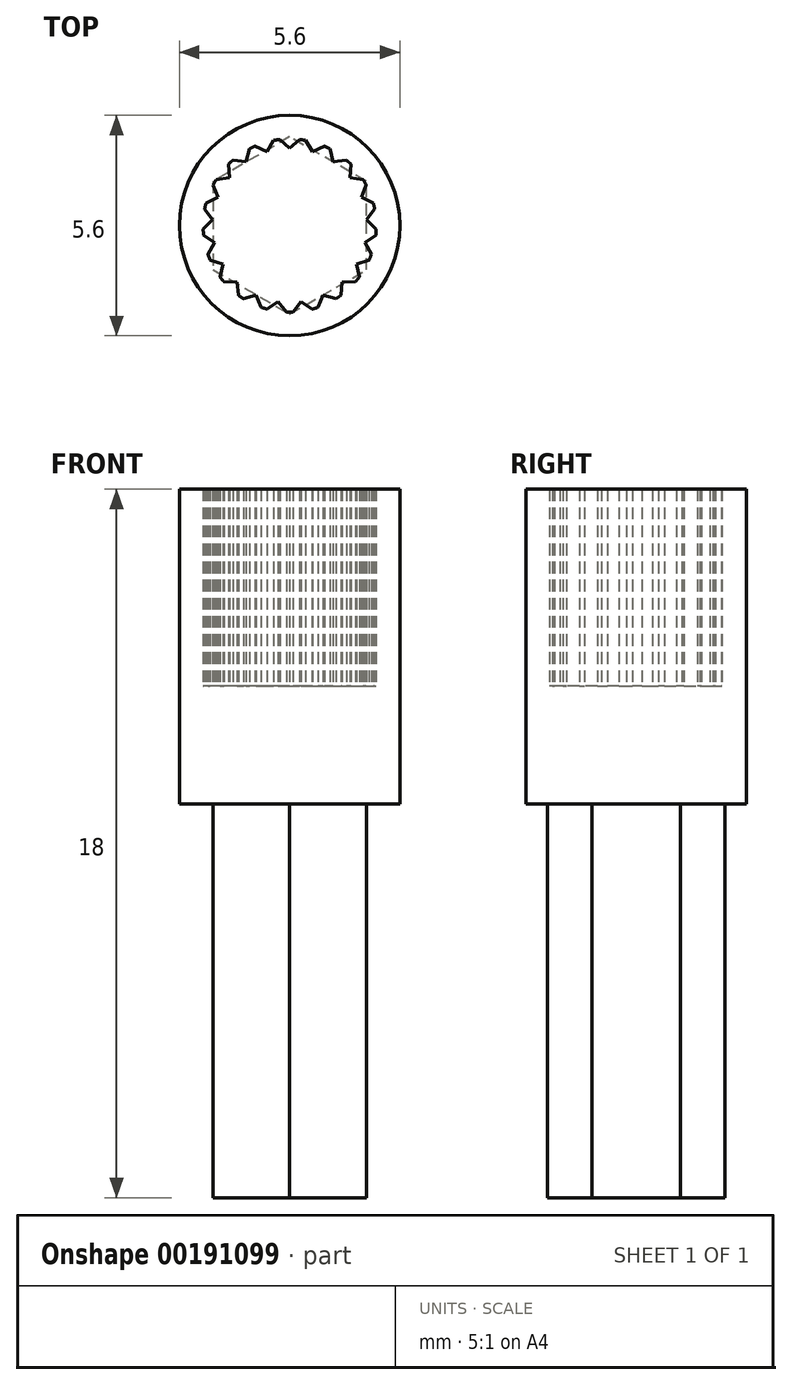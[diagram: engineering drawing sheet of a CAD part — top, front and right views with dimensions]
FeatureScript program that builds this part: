
annotation { "Feature Type Name" : "Feature", "Feature Type Description" : "" }
export const myFeature = defineFeature(function(context is Context, id is Id, definition is map)
    precondition{}
    {
        {
            var Q0;
            Q0=qCreatedBy(makeId("Top.planeOp"),FACE);
            var sketch = newSketch(context, id + "F0", { "sketchPlane" : qUnion([Q0])});
            skCircle(sketch, "E0", {"center": v(0, 0) * mm, "radius": 2.8 * mm});
            skLineSegment(sketch, "E1", {"start": v(0, 2.2) * mm, "end": v(0, 1.96) * mm, "construction": true});
            skArc(sketch, "E2", {"start": v(-0.25, 2.19) * mm, "mid": v(-0.33, 2.18) * mm, "end": v(-0.4, 2.16) * mm});
            skLineSegment(sketch, "E3", {"start": v(0, 1.96) * mm, "end": v(0.25, 2.19) * mm});
            skLineSegment(sketch, "E4.MirrorCS", {"start": v(0, 1.96) * mm, "end": v(-0.25, 2.19) * mm});
            skLineSegment(sketch, "E5.1.0", {"start": v(-0.58, 1.87) * mm, "end": v(-0.88, 2.01) * mm});
            skLineSegment(sketch, "E5.1.1", {"start": v(-0.58, 1.87) * mm, "end": v(-0.4, 2.16) * mm});
            skLineSegment(sketch, "E5.2.0", {"start": v(-1.1, 1.62) * mm, "end": v(-1.44, 1.66) * mm});
            skLineSegment(sketch, "E5.2.1", {"start": v(-1.1, 1.62) * mm, "end": v(-1.02, 1.95) * mm});
            skLineSegment(sketch, "E5.3.0", {"start": v(-1.53, 1.22) * mm, "end": v(-1.86, 1.17) * mm});
            skLineSegment(sketch, "E5.3.1", {"start": v(-1.53, 1.22) * mm, "end": v(-1.55, 1.56) * mm});
            skLineSegment(sketch, "E5.4.0", {"start": v(-1.82, 0.72) * mm, "end": v(-2.13, 0.57) * mm});
            skLineSegment(sketch, "E5.4.1", {"start": v(-1.82, 0.72) * mm, "end": v(-1.94, 1.03) * mm});
            skLineSegment(sketch, "E5.5.0", {"start": v(-1.95, 0.15) * mm, "end": v(-2.2, -0.09) * mm});
            skLineSegment(sketch, "E5.5.1", {"start": v(-1.95, 0.15) * mm, "end": v(-2.16, 0.41) * mm});
            skLineSegment(sketch, "E5.6.0", {"start": v(-1.91, -0.44) * mm, "end": v(-2.08, -0.73) * mm});
            skLineSegment(sketch, "E5.6.1", {"start": v(-1.91, -0.44) * mm, "end": v(-2.19, -0.24) * mm});
            skLineSegment(sketch, "E5.7.0", {"start": v(-1.7, -0.98) * mm, "end": v(-1.77, -1.3) * mm});
            skLineSegment(sketch, "E5.7.1", {"start": v(-1.7, -0.98) * mm, "end": v(-2.02, -0.88) * mm});
            skLineSegment(sketch, "E5.8.0", {"start": v(-1.33, -1.44) * mm, "end": v(-1.3, -1.77) * mm});
            skLineSegment(sketch, "E5.8.1", {"start": v(-1.33, -1.44) * mm, "end": v(-1.67, -1.43) * mm});
            skLineSegment(sketch, "E5.9.0", {"start": v(-0.85, -1.77) * mm, "end": v(-0.72, -2.08) * mm});
            skLineSegment(sketch, "E5.9.1", {"start": v(-0.85, -1.77) * mm, "end": v(-1.17, -1.86) * mm});
            skLineSegment(sketch, "E5.10.0", {"start": v(-0.3, -1.94) * mm, "end": v(-0.08, -2.2) * mm});
            skLineSegment(sketch, "E5.10.1", {"start": v(-0.3, -1.94) * mm, "end": v(-0.57, -2.12) * mm});
            skLineSegment(sketch, "E5.11.0", {"start": v(0.3, -1.94) * mm, "end": v(0.57, -2.12) * mm});
            skLineSegment(sketch, "E5.11.1", {"start": v(0.3, -1.94) * mm, "end": v(0.08, -2.2) * mm});
            skLineSegment(sketch, "E5.12.0", {"start": v(0.85, -1.77) * mm, "end": v(1.17, -1.86) * mm});
            skLineSegment(sketch, "E5.12.1", {"start": v(0.85, -1.77) * mm, "end": v(0.72, -2.08) * mm});
            skLineSegment(sketch, "E5.13.0", {"start": v(1.33, -1.44) * mm, "end": v(1.67, -1.43) * mm});
            skLineSegment(sketch, "E5.13.1", {"start": v(1.33, -1.44) * mm, "end": v(1.3, -1.77) * mm});
            skLineSegment(sketch, "E5.14.0", {"start": v(1.7, -0.98) * mm, "end": v(2.02, -0.88) * mm});
            skLineSegment(sketch, "E5.14.1", {"start": v(1.7, -0.98) * mm, "end": v(1.77, -1.3) * mm});
            skLineSegment(sketch, "E5.15.0", {"start": v(1.91, -0.44) * mm, "end": v(2.19, -0.24) * mm});
            skLineSegment(sketch, "E5.15.1", {"start": v(1.91, -0.44) * mm, "end": v(2.08, -0.73) * mm});
            skLineSegment(sketch, "E5.16.0", {"start": v(1.95, 0.15) * mm, "end": v(2.16, 0.41) * mm});
            skLineSegment(sketch, "E5.16.1", {"start": v(1.95, 0.15) * mm, "end": v(2.2, -0.09) * mm});
            skLineSegment(sketch, "E5.17.0", {"start": v(1.82, 0.72) * mm, "end": v(1.94, 1.03) * mm});
            skLineSegment(sketch, "E5.17.1", {"start": v(1.82, 0.72) * mm, "end": v(2.13, 0.57) * mm});
            skLineSegment(sketch, "E5.18.0", {"start": v(1.53, 1.22) * mm, "end": v(1.55, 1.56) * mm});
            skLineSegment(sketch, "E5.18.1", {"start": v(1.53, 1.22) * mm, "end": v(1.86, 1.17) * mm});
            skLineSegment(sketch, "E5.19.0", {"start": v(1.1, 1.62) * mm, "end": v(1.02, 1.95) * mm});
            skLineSegment(sketch, "E5.19.1", {"start": v(1.1, 1.62) * mm, "end": v(1.44, 1.66) * mm});
            skLineSegment(sketch, "E5.20.0", {"start": v(0.58, 1.87) * mm, "end": v(0.4, 2.16) * mm});
            skLineSegment(sketch, "E5.20.1", {"start": v(0.58, 1.87) * mm, "end": v(0.88, 2.01) * mm});
            skArc(sketch, "E6.trimOffspring", {"start": v(-0.88, 2.01) * mm, "mid": v(-0.95, 1.98) * mm, "end": v(-1.02, 1.95) * mm});
            skArc(sketch, "E7.trimOffspring", {"start": v(-1.44, 1.66) * mm, "mid": v(-1.5, 1.61) * mm, "end": v(-1.55, 1.56) * mm});
            skArc(sketch, "E8.trimOffspring", {"start": v(0.4, 2.16) * mm, "mid": v(0.33, 2.18) * mm, "end": v(0.25, 2.19) * mm});
            skArc(sketch, "E9.trimOffspring", {"start": v(1.02, 1.95) * mm, "mid": v(0.95, 1.98) * mm, "end": v(0.88, 2.01) * mm});
            skArc(sketch, "E10.trimOffspring", {"start": v(1.55, 1.56) * mm, "mid": v(1.5, 1.61) * mm, "end": v(1.44, 1.66) * mm});
            skArc(sketch, "E11.trimOffspring", {"start": v(1.94, 1.03) * mm, "mid": v(1.9, 1.1) * mm, "end": v(1.86, 1.17) * mm});
            skArc(sketch, "E12.trimOffspring", {"start": v(2.16, 0.41) * mm, "mid": v(2.14, 0.49) * mm, "end": v(2.13, 0.57) * mm});
            skArc(sketch, "E13.trimOffspring", {"start": v(2.19, -0.24) * mm, "mid": v(2.2, -0.16) * mm, "end": v(2.2, -0.09) * mm});
            skArc(sketch, "E14.trimOffspring", {"start": v(2.02, -0.88) * mm, "mid": v(2.05, -0.8) * mm, "end": v(2.08, -0.73) * mm});
            skArc(sketch, "E15.trimOffspring", {"start": v(1.67, -1.43) * mm, "mid": v(1.72, -1.37) * mm, "end": v(1.77, -1.3) * mm});
            skArc(sketch, "E16.trimOffspring", {"start": v(1.17, -1.86) * mm, "mid": v(1.24, -1.82) * mm, "end": v(1.3, -1.77) * mm});
            skArc(sketch, "E17.trimOffspring", {"start": v(0.57, -2.12) * mm, "mid": v(0.65, -2.1) * mm, "end": v(0.72, -2.08) * mm});
            skArc(sketch, "E18.trimOffspring", {"start": v(-0.08, -2.2) * mm, "mid": v(0, -2.2) * mm, "end": v(0.08, -2.2) * mm});
            skArc(sketch, "E19.trimOffspring", {"start": v(-0.72, -2.08) * mm, "mid": v(-0.65, -2.1) * mm, "end": v(-0.57, -2.12) * mm});
            skArc(sketch, "E20.trimOffspring", {"start": v(-1.3, -1.77) * mm, "mid": v(-1.24, -1.82) * mm, "end": v(-1.17, -1.86) * mm});
            skArc(sketch, "E21.trimOffspring", {"start": v(-1.77, -1.3) * mm, "mid": v(-1.72, -1.37) * mm, "end": v(-1.67, -1.43) * mm});
            skArc(sketch, "E22.trimOffspring", {"start": v(-2.08, -0.73) * mm, "mid": v(-2.05, -0.8) * mm, "end": v(-2.02, -0.88) * mm});
            skArc(sketch, "E23.trimOffspring", {"start": v(-2.2, -0.09) * mm, "mid": v(-2.2, -0.16) * mm, "end": v(-2.19, -0.24) * mm});
            skArc(sketch, "E24.trimOffspring", {"start": v(-2.13, 0.57) * mm, "mid": v(-2.14, 0.49) * mm, "end": v(-2.16, 0.41) * mm});
            skArc(sketch, "E25.trimOffspring", {"start": v(-1.86, 1.17) * mm, "mid": v(-1.9, 1.1) * mm, "end": v(-1.94, 1.03) * mm});
            skSolve(sketch);
        }
        {
            var Q0;
            Q0 = qSketchRegion(id + "F0", true);
            extrude(context, id + "F1", {"entities" : qUnion([Q0]), "depth" : 5 * mm});
        }
        {
            var Q0;
            Q0=makeQuery(id+"F0.imprint","IMPRINT",FACE,{"disambiguationData":[TD([[makeQuery(id+"F0.imprint","IMPRINT",EDGE,{"derivedFrom":sQuery(id+"F0.wireOp",EDGE,"E2")}),1.0]])]});
            var Q1;
            Q1=makeQuery(id+"F0.imprint","IMPRINT",FACE,{"disambiguationData":[TD([[makeQuery(id+"F0.imprint","IMPRINT",EDGE,{"derivedFrom":sQuery(id+"F0.wireOp",EDGE,"E0")}),1.0]])]});
            extrude(context, id + "F2", {"entities" : qUnion([Q0, Q1]), "operationType" : NewBodyOperationType.ADD, "oppositeDirection" : true, "depth" : 3 * mm});
        }
        {
            var Q0;
            Q0=makeQuery(id+"F2.opExtrude","CAP_FACE",FACE,{"disambiguationData":[OSD([sQuery(id+"F0.wireOp",EDGE,"E0")])],"isStart":false});
            var sketch = newSketch(context, id + "F3", { "sketchPlane" : qUnion([Q0])});
            skCircle(sketch, "E26.cCircle", {"center": v(0, 0) * mm, "radius": 1.95 * mm, "construction": true});
            skLineSegment(sketch, "E26.0", {"start": v(1.95, 1.13) * mm, "end": v(1.95, -1.13) * mm});
            skLineSegment(sketch, "E26.1", {"start": v(1.95, -1.13) * mm, "end": v(0, -2.25) * mm});
            skLineSegment(sketch, "E26.2", {"start": v(0, -2.25) * mm, "end": v(-1.95, -1.13) * mm});
            skLineSegment(sketch, "E26.3", {"start": v(-1.95, -1.13) * mm, "end": v(-1.95, 1.13) * mm});
            skLineSegment(sketch, "E26.4", {"start": v(-1.95, 1.13) * mm, "end": v(0, 2.25) * mm});
            skLineSegment(sketch, "E26.5", {"start": v(0, 2.25) * mm, "end": v(1.95, 1.13) * mm});
            skPoint(sketch, "E26.0.midPoint", {"position": v(1.95, 0) * mm});
            skSolve(sketch);
        }
        {
            var Q0;
            Q0 = qSketchRegion(id + "F3", true);
            extrude(context, id + "F4", {"entities" : qUnion([Q0]), "operationType" : NewBodyOperationType.ADD, "depth" : 10 * mm});
        }
    });
